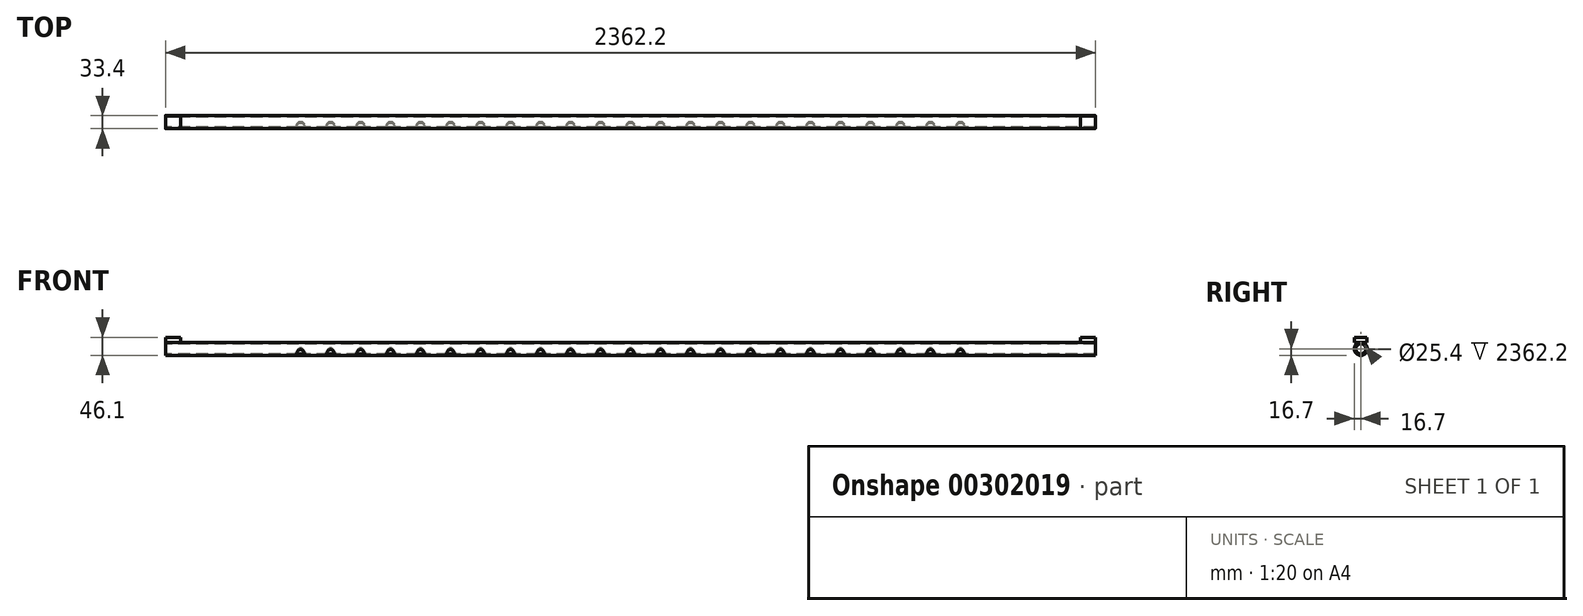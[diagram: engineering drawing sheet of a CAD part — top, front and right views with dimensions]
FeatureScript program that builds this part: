
annotation { "Feature Type Name" : "Feature", "Feature Type Description" : "" }
export const myFeature = defineFeature(function(context is Context, id is Id, definition is map)
    precondition{}
    {
        {
            var Q0;
            Q0=qCreatedBy(makeId("Right.planeOp"),FACE);
            var sketch = newSketch(context, id + "F0", { "sketchPlane" : qUnion([Q0])});
            skCircle(sketch, "E0", {"center": v(0, 0) * mm, "radius": 16.7 * mm});
            skCircle(sketch, "E1", {"center": v(0, 0) * mm, "radius": 12.7 * mm});
            skSolve(sketch);
        }
        {
            var Q0;
            Q0 = qSketchRegion(id + "F0", true);
            extrude(context, id + "F1", {"entities" : qUnion([Q0]), "endBound" : BoundingType.SYMMETRIC, "depth" : 2362.2 * mm});
        }
        {
            var Q0;
            Q0=qCreatedBy(makeId("Top.planeOp"),FACE);
            cPlane(context, id + "F2", {"entities" : qUnion([Q0]), "cplaneType" : CPlaneType.OFFSET, "offset" : 16.7 * mm, "width" : 152.4 * mm, "height" : 152.4 * mm});
        }
        {
            var Q0;
            Q0=qCreatedBy(id+"F2.planeOp",FACE);
            var sketch = newSketch(context, id + "F3", { "sketchPlane" : qUnion([Q0])});
            skLineSegment(sketch, "E2", {"start": v(0, 113.47) * mm, "end": v(0, -135.26) * mm, "construction": true});
            skLineSegment(sketch, "E3", {"start": v(-1283.9, 0) * mm, "end": v(1277.96, 0) * mm, "construction": true});
            skPoint(sketch, "E4", {"position": v(0, 0) * mm});
            skPoint(sketch, "E5.1.0.0", {"position": v(76.2, 0) * mm});
            skPoint(sketch, "E5.2.0.0", {"position": v(152.4, 0) * mm});
            skPoint(sketch, "E5.3.0.0", {"position": v(228.6, 0) * mm});
            skPoint(sketch, "E5.4.0.0", {"position": v(304.8, 0) * mm});
            skPoint(sketch, "E5.5.0.0", {"position": v(381, 0) * mm});
            skPoint(sketch, "E5.6.0.0", {"position": v(457.2, 0) * mm});
            skPoint(sketch, "E5.7.0.0", {"position": v(533.4, 0) * mm});
            skPoint(sketch, "E5.8.0.0", {"position": v(609.6, 0) * mm});
            skPoint(sketch, "E5.9.0.0", {"position": v(685.8, 0) * mm});
            skLineSegment(sketch, "E5.direction1", {"start": v(0, 0) * mm, "end": v(76.2, 0) * mm, "construction": true});
            skLineSegment(sketch, "E6.0", {"start": v(965.2, 113.47) * mm, "end": v(965.2, -135.26) * mm, "construction": true});
            skPoint(sketch, "E7.0.10.0", {"position": v(762, 0) * mm});
            skPoint(sketch, "E7.0.11.0", {"position": v(838.2, 0) * mm});
            skPoint(sketch, "E8.1.0.0", {"position": v(-76.2, 0) * mm});
            skPoint(sketch, "E8.2.0.0", {"position": v(-152.4, 0) * mm});
            skPoint(sketch, "E8.3.0.0", {"position": v(-228.6, 0) * mm});
            skPoint(sketch, "E8.4.0.0", {"position": v(-304.8, 0) * mm});
            skPoint(sketch, "E8.5.0.0", {"position": v(-381, 0) * mm});
            skPoint(sketch, "E8.6.0.0", {"position": v(-457.2, 0) * mm});
            skPoint(sketch, "E8.7.0.0", {"position": v(-533.4, 0) * mm});
            skPoint(sketch, "E8.8.0.0", {"position": v(-609.6, 0) * mm});
            skPoint(sketch, "E8.9.0.0", {"position": v(-685.8, 0) * mm});
            skPoint(sketch, "E8.10.0.0", {"position": v(-762, 0) * mm});
            skPoint(sketch, "E8.11.0.0", {"position": v(-838.2, 0) * mm});
            skLineSegment(sketch, "E8.direction1", {"start": v(0, 0) * mm, "end": v(-76.2, 0) * mm, "construction": true});
            skSolve(sketch);
        }
        {
            var Q0;
            Q0=sQuery(id+"F3.wireOp",VERTEX,"E8.11.0.0");
            var Q1;
            Q1=sQuery(id+"F3.wireOp",VERTEX,"E8.10.0.0");
            var Q2;
            Q2=sQuery(id+"F3.wireOp",VERTEX,"E8.9.0.0");
            var Q3;
            Q3=sQuery(id+"F3.wireOp",VERTEX,"E8.8.0.0");
            var Q4;
            Q4=sQuery(id+"F3.wireOp",VERTEX,"E8.7.0.0");
            var Q5;
            Q5=sQuery(id+"F3.wireOp",VERTEX,"E8.6.0.0");
            var Q6;
            Q6=sQuery(id+"F3.wireOp",VERTEX,"E8.5.0.0");
            var Q7;
            Q7=sQuery(id+"F3.wireOp",VERTEX,"E8.4.0.0");
            var Q8;
            Q8=sQuery(id+"F3.wireOp",VERTEX,"E8.3.0.0");
            var Q9;
            Q9=sQuery(id+"F3.wireOp",VERTEX,"E8.2.0.0");
            var Q10;
            Q10=sQuery(id+"F3.wireOp",VERTEX,"E8.1.0.0");
            var Q11;
            Q11=sQuery(id+"F3.wireOp",VERTEX,"E4");
            var Q12;
            Q12=sQuery(id+"F3.wireOp",VERTEX,"E5.1.0.0");
            var Q13;
            Q13=sQuery(id+"F3.wireOp",VERTEX,"E5.2.0.0");
            var Q14;
            Q14=sQuery(id+"F3.wireOp",VERTEX,"E5.3.0.0");
            var Q15;
            Q15=sQuery(id+"F3.wireOp",VERTEX,"E5.4.0.0");
            var Q16;
            Q16=sQuery(id+"F3.wireOp",VERTEX,"E5.5.0.0");
            var Q17;
            Q17=sQuery(id+"F3.wireOp",VERTEX,"E5.6.0.0");
            var Q18;
            Q18=sQuery(id+"F3.wireOp",VERTEX,"E5.7.0.0");
            var Q19;
            Q19=sQuery(id+"F3.wireOp",VERTEX,"E5.8.0.0");
            var Q20;
            Q20=sQuery(id+"F3.wireOp",VERTEX,"E5.9.0.0");
            var Q21;
            Q21=sQuery(id+"F3.wireOp",VERTEX,"E7.0.10.0");
            var Q22;
            Q22=sQuery(id+"F3.wireOp",VERTEX,"E7.0.11.0");
            var Q23;
            Q23=makeQuery(id+"F1.opExtrude","SWEPT_BODY",BODY,{"disambiguationData":[OSD([sQuery(id+"F0.wireOp",EDGE,"E0"),sQuery(id+"F0.wireOp",EDGE,"E1")])]});
            hole(context, id + "F4", {"style" : HoleStyle.SIMPLE, "endStyle" : HoleEndStyle.BLIND, "holeDiameter" : 20.57 * mm, "holeDepth" : 12.7 * mm, "tappedDepth" : 24.13 * mm, "tapClearance" : 3, "startFromSketch" : true, "locations" : qUnion([Q0, Q1, Q2, Q3, Q4, Q5, Q6, Q7, Q8, Q9, Q10, Q11, Q12, Q13, Q14, Q15, Q16, Q17, Q18, Q19, Q20, Q21, Q22]), "scope" : qUnion([Q23])});
        }
        {
            var Q0;
            Q0=qCreatedBy(makeId("Top.planeOp"),FACE);
            var sketch = newSketch(context, id + "F5", { "sketchPlane" : qUnion([Q0])});
            skLineSegment(sketch, "E9", {"start": v(-1480.6, 0) * mm, "end": v(1384.83, 0) * mm, "construction": true});
            skSolve(sketch);
        }
        {
            var Q0;
            Q0=makeQuery(id+"F1.opExtrude","SWEPT_BODY",BODY,{"disambiguationData":[OSD([sQuery(id+"F0.wireOp",EDGE,"E0"),sQuery(id+"F0.wireOp",EDGE,"E1")])]});
            var Q1;
            Q1=sQuery(id+"F5.wireOp",EDGE,"E9");
            transform(context, id + "F6", {"entities" : qUnion([Q0]), "transformType" : TransformType.ROTATION, "transformAxis" : qUnion([Q1]), "angle" : 135 * degree, "makeCopy" : false});
        }
        {
            var Q0;
            Q0=makeQuery(id+"F1.opExtrude","CAP_FACE",FACE,{"disambiguationData":[OSD([sQuery(id+"F0.wireOp",EDGE,"E0"),sQuery(id+"F0.wireOp",EDGE,"E1")])],"isStart":false});
            var sketch = newSketch(context, id + "F7", { "sketchPlane" : qUnion([Q0])});
            skLineSegment(sketch, "E10", {"start": v(0, 0) * mm, "end": v(0, 32.37) * mm, "construction": true});
            skLineSegment(sketch, "E11.0", {"start": v(15.88, 0) * mm, "end": v(15.88, 32.37) * mm, "construction": true});
            skLineSegment(sketch, "E12", {"start": v(-61.16, 0) * mm, "end": v(62.55, 0) * mm, "construction": true});
            skLineSegment(sketch, "E13.0", {"start": v(-61.16, 16.7) * mm, "end": v(62.55, 16.7) * mm, "construction": true});
            skLineSegment(sketch, "E14.bottom", {"start": v(15.88, 16.7) * mm, "end": v(-15.88, 16.7) * mm});
            skLineSegment(sketch, "E14.top", {"start": v(15.88, 29.4) * mm, "end": v(-15.88, 29.4) * mm});
            skLineSegment(sketch, "E14.left", {"start": v(15.88, 16.7) * mm, "end": v(15.88, 29.4) * mm});
            skLineSegment(sketch, "E14.right", {"start": v(-15.88, 16.7) * mm, "end": v(-15.88, 29.4) * mm});
            skSolve(sketch);
        }
        {
            var Q0;
            Q0 = qSketchRegion(id + "F7", true);
            extrude(context, id + "F8", {"entities" : qUnion([Q0]), "oppositeDirection" : true, "depth" : 38.1 * mm});
        }
        {
            var Q0;
            Q0=makeQuery(id+"F8.opExtrude","SWEPT_BODY",BODY,{"disambiguationData":[OSD([sQuery(id+"F7.wireOp",EDGE,"E14.bottom"),sQuery(id+"F7.wireOp",EDGE,"E14.top"),sQuery(id+"F7.wireOp",EDGE,"E14.left"),sQuery(id+"F7.wireOp",EDGE,"E14.right")])]});
            var Q1;
            Q1=qCreatedBy(makeId("Right.planeOp"),FACE);
            mirror(context, id + "F9", {"entities" : qUnion([Q0]), "mirrorPlane" : qUnion([Q1])});
        }
    });
